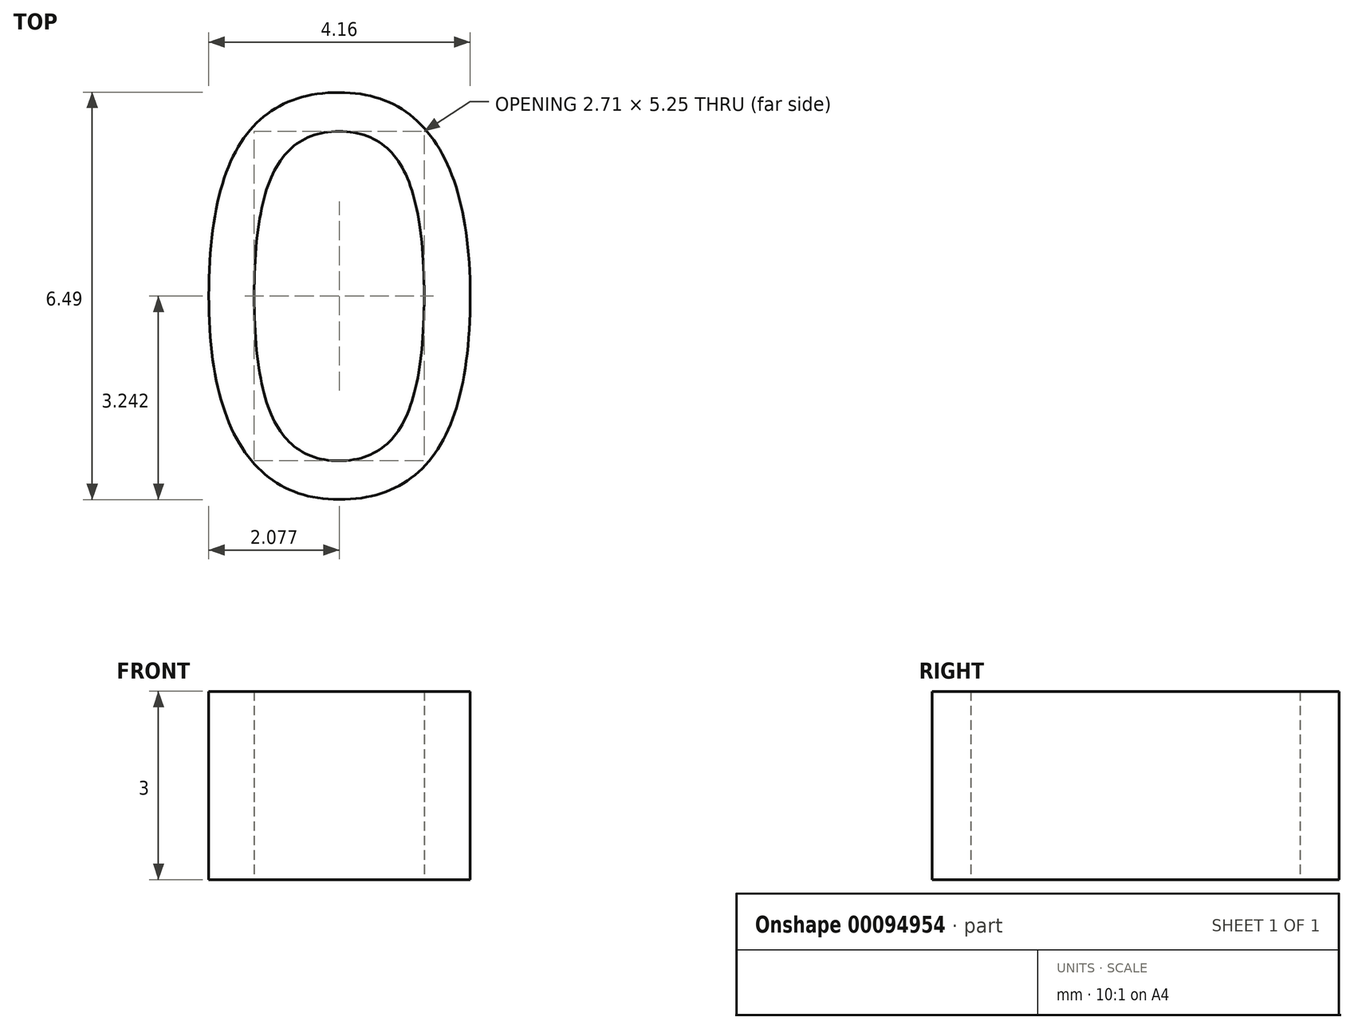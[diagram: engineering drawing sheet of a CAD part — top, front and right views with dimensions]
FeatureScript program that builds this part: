
annotation { "Feature Type Name" : "Feature", "Feature Type Description" : "" }
export const myFeature = defineFeature(function(context is Context, id is Id, definition is map)
    precondition{}
    {
        {
            var Q0;
            Q0=qCreatedBy(makeId("Top.planeOp"),FACE);
            var sketch = newSketch(context, id + "F0", { "sketchPlane" : qUnion([Q0])});
            skText(sketch, "E0", { "text": "0", "fontName": "OpenSans-Regular.ttf"});
            const initialGuessF0  = {"E0": [-0.00337, -0.00387, 1, 0, 0.00635]};
            skSetInitialGuess(sketch, initialGuessF0);
            skSolve(sketch);
        }
        {
            var Q0;
            Q0 = qSketchRegion(id + "F0", true);
            extrude(context, id + "F1", {"entities" : qUnion([Q0]), "depth" : 3 * mm});
        }
    });
